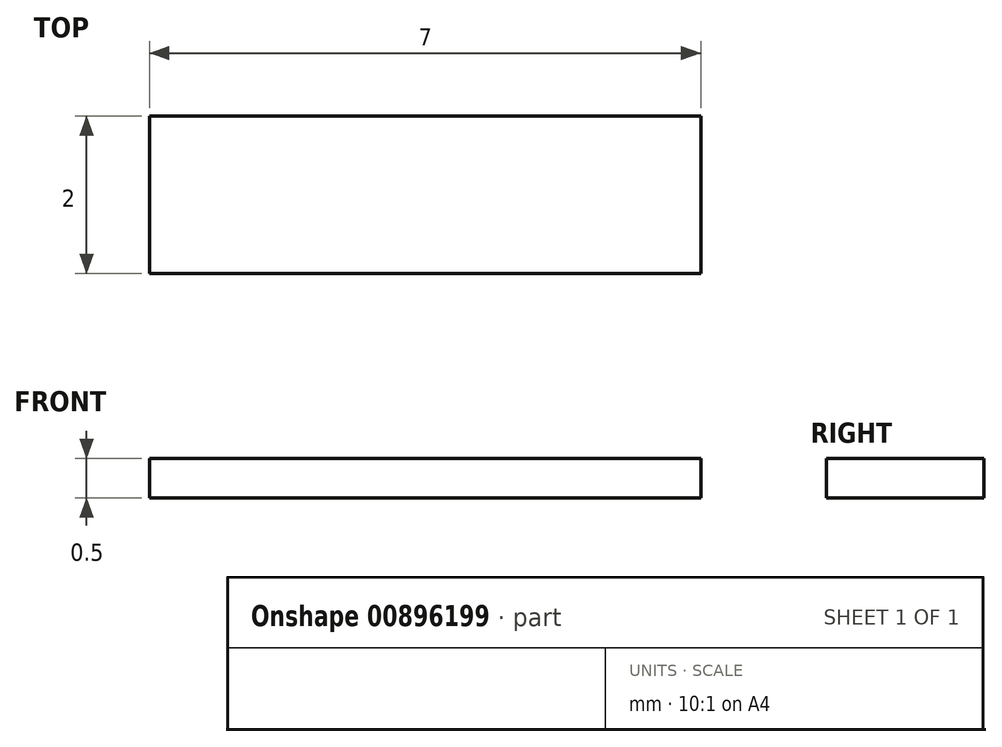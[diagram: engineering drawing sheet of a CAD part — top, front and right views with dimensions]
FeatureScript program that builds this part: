
annotation { "Feature Type Name" : "Feature", "Feature Type Description" : "" }
export const myFeature = defineFeature(function(context is Context, id is Id, definition is map)
    precondition{}
    {
        {
            var Q0;
            Q0=qCreatedBy(makeId("Top.planeOp"),FACE);
            var sketch = newSketch(context, id + "F0", { "sketchPlane" : qUnion([Q0])});
            skLineSegment(sketch, "E0.bottom", {"start": v(0, 0) * mm, "end": v(7, 0) * mm});
            skLineSegment(sketch, "E0.top", {"start": v(0, 2) * mm, "end": v(7, 2) * mm});
            skLineSegment(sketch, "E0.left", {"start": v(0, 0) * mm, "end": v(0, 2) * mm});
            skLineSegment(sketch, "E0.right", {"start": v(7, 0) * mm, "end": v(7, 2) * mm});
            skSolve(sketch);
        }
        {
            var Q0;
            Q0=makeQuery(id+"F0.imprint","IMPRINT",FACE,{"disambiguationData":[TD([[makeQuery(id+"F0.imprint","IMPRINT",EDGE,{"derivedFrom":sQuery(id+"F0.wireOp",EDGE,"E0.bottom")}),1.0]])]});
            extrude(context, id + "F1", {"entities" : qUnion([Q0]), "depth" : 0.5 * mm, "offsetDistance" : 25 * mm});
        }
    });
